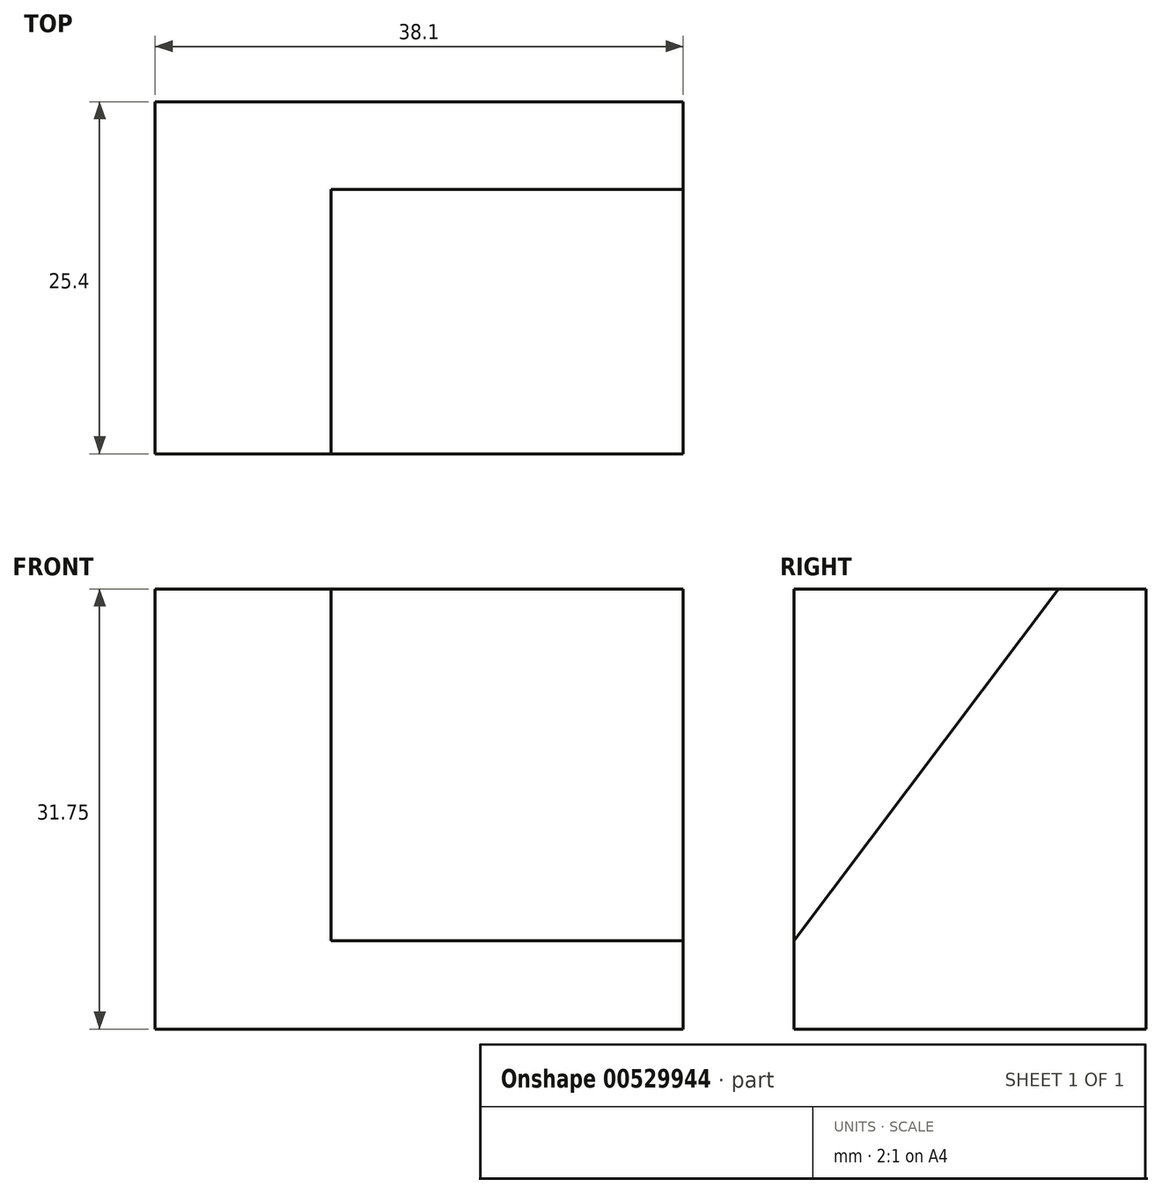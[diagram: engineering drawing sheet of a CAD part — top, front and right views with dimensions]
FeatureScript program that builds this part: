
annotation { "Feature Type Name" : "Feature", "Feature Type Description" : "" }
export const myFeature = defineFeature(function(context is Context, id is Id, definition is map)
    precondition{}
    {
        {
            var Q0;
            Q0=qCreatedBy(makeId("Front.planeOp"),FACE);
            var sketch = newSketch(context, id + "F0", { "sketchPlane" : qUnion([Q0])});
            skLineSegment(sketch, "E0.bottom", {"start": v(-64.1, 58.56) * mm, "end": v(-26, 58.56) * mm});
            skLineSegment(sketch, "E0.top", {"start": v(-64.1, 26.8) * mm, "end": v(-26, 26.8) * mm});
            skLineSegment(sketch, "E0.left", {"start": v(-64.1, 58.56) * mm, "end": v(-64.1, 26.8) * mm});
            skLineSegment(sketch, "E0.right", {"start": v(-26, 58.56) * mm, "end": v(-26, 26.8) * mm});
            skSolve(sketch);
        }
        {
            var Q0;
            Q0=makeQuery(id+"F0.imprint","IMPRINT",FACE,{"disambiguationData":[TD([[makeQuery(id+"F0.imprint","IMPRINT",EDGE,{"derivedFrom":sQuery(id+"F0.wireOp",EDGE,"E0.bottom")}),-1.0]])]});
            extrude(context, id + "F1", {"entities" : qUnion([Q0]), "depth" : 25.4 * mm, "offsetDistance" : 25.4 * mm});
        }
        {
            var Q0;
            Q0=makeQuery(id+"F1.opExtrude","SWEPT_FACE",FACE,{"disambiguationData":[OSD([sQuery(id+"F0.wireOp",EDGE,"E0.right")])]});
            var sketch = newSketch(context, id + "F2", { "sketchPlane" : qUnion([Q0])});
            skLineSegment(sketch, "E1", {"start": v(-25.4, 26.8) * mm, "end": v(-25.4, 33.17) * mm});
            skLineSegment(sketch, "E2", {"start": v(-25.4, 33.17) * mm, "end": v(-6.33, 58.56) * mm});
            skLineSegment(sketch, "E3", {"start": v(-6.33, 58.56) * mm, "end": v(0, 58.56) * mm});
            skLineSegment(sketch, "E4", {"start": v(0, 58.56) * mm, "end": v(0, 26.8) * mm});
            skLineSegment(sketch, "E5", {"start": v(0, 26.8) * mm, "end": v(-25.4, 26.8) * mm});
            skSolve(sketch);
        }
        {
            var Q0;
            {var subQ0=sQuery(id+"F2.wireOp",EDGE,"E2");Q0=makeQuery(id+"F2.imprint","IMPRINT",FACE,{"disambiguationData":[TD([[makeQuery(id+"F2.imprint","IMPRINT",EDGE,{"derivedFrom":subQ0}),1.0]])]});}
            extrude(context, id + "F3", {"entities" : qUnion([Q0]), "operationType" : NewBodyOperationType.REMOVE, "oppositeDirection" : true, "depth" : 25.4 * mm, "offsetDistance" : 25.4 * mm});
        }
    });
